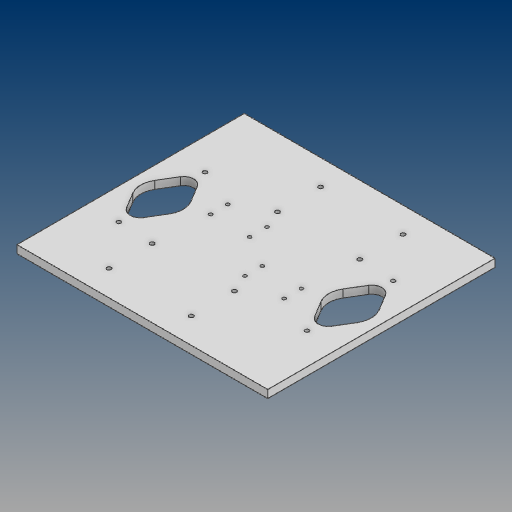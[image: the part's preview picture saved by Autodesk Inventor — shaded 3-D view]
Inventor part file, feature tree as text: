
AUTODESK INVENTOR PART (.ipt)
format: ipt  version: 2021 (Build 250183000, 183)  size: 181,248 bytes
history: native  units: mm
features: reference x17, other x6, sketch x5, hole x3, extrude x2, mirror x1, projected_geometry x1
ambient origin geometry x8: Origin, YZ Plane, XZ Plane, XY Plane, X Axis, Y Axis, Z Axis, Center Point
bodies: Solid1 (feature_tree)
feature tree (35):
  extrude  "Extrusion1"  Depth=320.0mm
  extrude  "Extrusion2"  Depth=54.0mm
  hole  "Hole2"  [1 undecoded]
  mirror  "Mirror1"
  hole  "Hole3"  [1 undecoded]
  hole  "Hole4"  [1 undecoded]
  sketch  "Sketch1"  dims[d0=290.0mm d1=320.0mm]
  sketch  "Sketch3"  dims[d2=10.0mm d3=0.0mm d13=54.0mm]
  sketch  "Sketch4"  dims[d14=25.0mm d15=25.0mm d16=0.0mm]
  projected_geometry  "Projected Loop2"
  sketch  "Sketch5"  dims[d17=55.0mm]
  reference  "Reference1"
  reference  "Reference2"
  reference  "Reference3"
  reference  "Reference4"
  reference  "Reference5"
  reference  "Reference6"
  reference  "Reference7"
  reference  "Reference8"
  reference  "Reference9"
  sketch  "Sketch6"  dims[d18=5.2mm d19=6.0mm d20=4.0mm d21=2.0mm d22=90.0deg d23=8.0mm d24=20.594885mm d25=5.5mm d26=6.0mm d27=4.0mm d28=2.0mm d29=90.0deg d30=8.0mm d31=20.594885mm d32=4.4mm d33=6.0mm d34=4.0mm d35=2.0mm d36=90.0deg d37=8.0mm d38=20.594885mm]
  reference  "Reference10"
  reference  "Reference11"
  reference  "Reference12"
  reference  "Reference13"
  reference  "Reference14"
  reference  "Reference15"
  reference  "Reference16"
  reference  "Reference17"
  other  "0002_Part_De_xe.iam"
  other  "0001_ASS_Hop_so:1"
  other  "22_Hop_so_ngang:2"
  other  "22_Hop_so_ngang:1"
  other  "0001_ASS_Hop_so:2"
  other  "08_Ga_dong_co_02:1"
note: 3 required parameter values undecoded (feature->parameter linkage not recoverable at this tier; creation-order binding heuristic only, values carry confidence <= 0.55)
